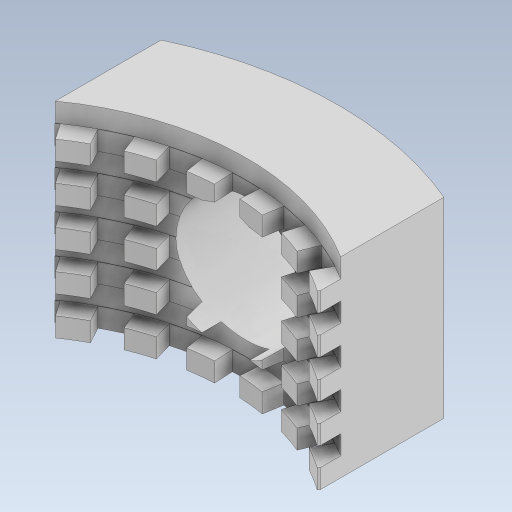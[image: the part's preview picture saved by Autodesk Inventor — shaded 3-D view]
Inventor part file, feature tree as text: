
AUTODESK INVENTOR PART (.ipt)
format: ipt  version: 2023 (Build 270158000, 158)  size: 897,024 bytes
history: native  units: in
note: dims shown in document units (in); Inventor stores cm internally (conversion verified against a paired STEP export)
features: sketch x7, extrude x6, revolve x1, plane x1, projected_geometry x1
ambient origin geometry x8: Origin, YZ Plane, XZ Plane, XY Plane, X Axis, Y Axis, Z Axis, Center Point
bodies: Solid1 (feature_tree)
feature tree (16):
  extrude  "Extrusion1"  Depth=0.2362in TaperAngle=0.0deg
  extrude  "Extrusion2"  Depth=0.3937in TaperAngle=0.0deg
  extrude  "Extrusion3"  Depth=0.0394in TaperAngle=120.0deg
  revolve  "Revolution1"  [1 undecoded]
  extrude  "Extrusion13"  Depth=0.2362in TaperAngle=0.0deg
  plane  "Work Plane5"
  extrude  "Extrusion14"  TaperAngle=0.0deg  [1 undecoded]
  extrude  "Extrusion15"  TaperAngle=0.0deg  [1 undecoded]
  sketch  "Sketch1"  dims[d0=1.0236in d1=0.2362in d2=0.0in]
  sketch  "Sketch2"  dims[d3=120.0deg d4=0.3937in d5=0.0in]
  sketch  "Sketch3"  dims[d6=0.0394in d7=7.874in d9=120.0deg]
  sketch  "Sketch4"  dims[d11=0.3937in d12=0.0in d14=3.937in d16=0.0394in d17=0.3937in d19=0.3937in]
  sketch  "Sketch25"  dims[d21=360.0deg d105=0.2362in d106=0.0in]
  projected_geometry  "Projected Loop9"
  sketch  "Sketch26"  dims[d107=0.2559in d108=0.0in d109=0.0in]
  sketch  "Sketch27"  dims[d110=0.5709in d111=0.0in d112=0.0in d91=0.0344in d92=0.0344in d93=0.0197in d94=0.0344in]
note: 3 required parameter values undecoded (feature->parameter linkage not recoverable at this tier; creation-order binding heuristic only, values carry confidence <= 0.55)